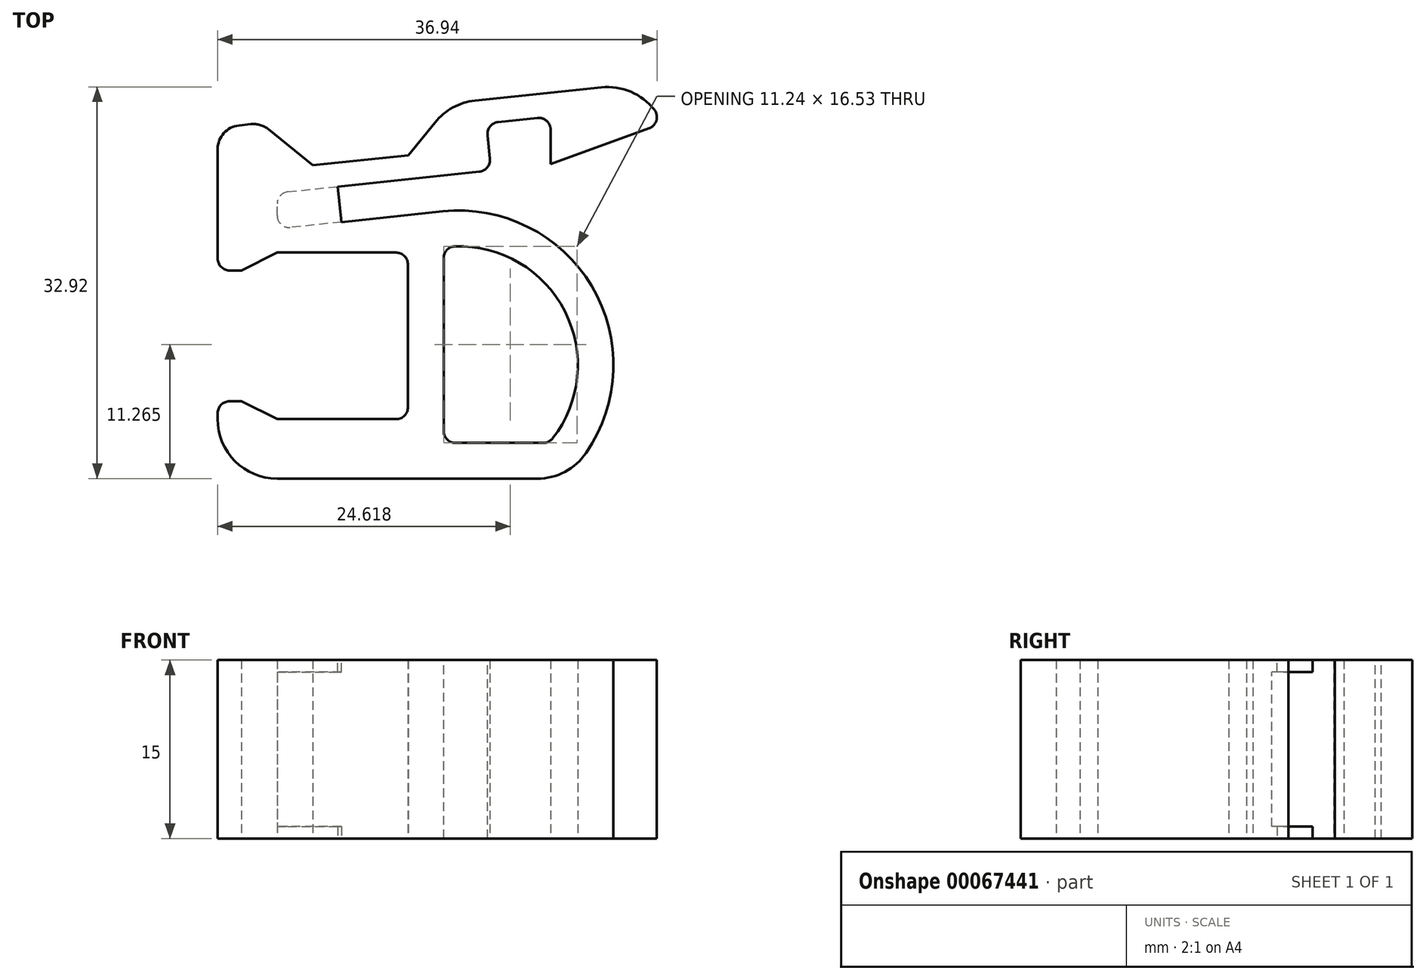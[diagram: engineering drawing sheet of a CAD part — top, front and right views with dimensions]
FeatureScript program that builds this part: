
annotation { "Feature Type Name" : "Feature", "Feature Type Description" : "" }
export const myFeature = defineFeature(function(context is Context, id is Id, definition is map)
    precondition{}
    {
        {
            var Q0;
            Q0=qCreatedBy(makeId("Top.planeOp"),FACE);
            var sketch = newSketch(context, id + "F0", { "sketchPlane" : qUnion([Q0])});
            skLineSegment(sketch, "E0", {"start": v(12, 7.43) * mm, "end": v(21.4, 10.85) * mm});
            skLineSegment(sketch, "E1", {"start": v(21.4, 10.85) * mm, "end": v(21.4, 14.43) * mm});
            skLineSegment(sketch, "E2", {"start": v(21.4, 14.43) * mm, "end": v(3.58, 12.56) * mm});
            skLineSegment(sketch, "E3", {"start": v(-16, 10.5) * mm, "end": v(-16, -1.5) * mm});
            skLineSegment(sketch, "E4", {"start": v(-16, -1.5) * mm, "end": v(-14, -1.5) * mm});
            skLineSegment(sketch, "E5", {"start": v(-14, -1.5) * mm, "end": v(-11, 0) * mm});
            skLineSegment(sketch, "E6", {"start": v(-11, 0) * mm, "end": v(0, 0) * mm});
            skLineSegment(sketch, "E7", {"start": v(0, 0) * mm, "end": v(0, -14) * mm});
            skLineSegment(sketch, "E8", {"start": v(0, -14) * mm, "end": v(-11, -14) * mm});
            skLineSegment(sketch, "E9", {"start": v(-11, -14) * mm, "end": v(-14, -12.5) * mm});
            skLineSegment(sketch, "E10", {"start": v(-14, -12.5) * mm, "end": v(-16, -12.5) * mm});
            skLineSegment(sketch, "E11", {"start": v(-16, -12.5) * mm, "end": v(-16, -19) * mm});
            skLineSegment(sketch, "E12", {"start": v(-16, -19) * mm, "end": v(13.12, -19) * mm});
            skLineSegment(sketch, "E13", {"start": v(2.92, 3.46) * mm, "end": v(-11, 2) * mm});
            skLineSegment(sketch, "E14", {"start": v(-11, 2) * mm, "end": v(-11, 5.02) * mm});
            skLineSegment(sketch, "E15", {"start": v(-11, 5.02) * mm, "end": v(7, 6.9) * mm});
            skLineSegment(sketch, "E16", {"start": v(7, 6.9) * mm, "end": v(6.58, 10.86) * mm});
            skLineSegment(sketch, "E17", {"start": v(6.58, 10.86) * mm, "end": v(12, 11.43) * mm});
            skLineSegment(sketch, "E18", {"start": v(12, 11.43) * mm, "end": v(12, 7.43) * mm});
            skArc(sketch, "E19", {"start": v(13.12, -19) * mm, "mid": v(16.12, -4.1) * mm, "end": v(2.92, 3.46) * mm});
            skArc(sketch, "E20.0", {"start": v(11.85, -16) * mm, "mid": v(13.09, -4.73) * mm, "end": v(3, 0.45) * mm});
            skLineSegment(sketch, "E21", {"start": v(3, 0.45) * mm, "end": v(3, -16) * mm});
            skLineSegment(sketch, "E22", {"start": v(3, -16) * mm, "end": v(11.85, -16) * mm});
            skLineSegment(sketch, "E23", {"start": v(-12.37, 10.88) * mm, "end": v(-8, 7.34) * mm});
            skLineSegment(sketch, "E24", {"start": v(-8, 7.34) * mm, "end": v(0.04, 8.19) * mm});
            skLineSegment(sketch, "E25", {"start": v(0.04, 8.19) * mm, "end": v(3.58, 12.56) * mm});
            skLineSegment(sketch, "E26.trimOffspring", {"start": v(-12.37, 10.88) * mm, "end": v(-16, 10.5) * mm});
            skSolve(sketch);
        }
        {
            var Q0;
            Q0=qSketchRegion(id+"F0",true);
            extrude(context, id + "F1", {"entities" : qUnion([Q0]), "endBound" : BoundingType.SYMMETRIC, "depth" : 15 * mm});
        }
        {
            var Q0;
            Q0=makeQuery(id+"F1.opExtrude","SWEPT_EDGE",EDGE,{"disambiguationData":[OSD([sQuery(id+"F0.wireOp",EDGE,"E1"),sQuery(id+"F0.wireOp",EDGE,"E2")])]});
            var Q1;
            Q1=makeQuery(id+"F1.opExtrude","SWEPT_EDGE",EDGE,{"disambiguationData":[OSD([sQuery(id+"F0.wireOp",EDGE,"E2"),sQuery(id+"F0.wireOp",EDGE,"E25")])]});
            var Q2;
            Q2=makeQuery(id+"F1.opExtrude","SWEPT_EDGE",EDGE,{"disambiguationData":[OSD([sQuery(id+"F0.wireOp",EDGE,"E1"),sQuery(id+"F0.wireOp",EDGE,"E2")])]});
            var Q3;
            Q3=makeQuery(id+"F1.opExtrude","SWEPT_EDGE",EDGE,{"disambiguationData":[OSD([sQuery(id+"F0.wireOp",EDGE,"E11"),sQuery(id+"F0.wireOp",EDGE,"E12")])]});
            var Q4;
            Q4=makeQuery(id+"F1.opExtrude","SWEPT_EDGE",EDGE,{"disambiguationData":[OSD([sQuery(id+"F0.wireOp",EDGE,"E12"),sQuery(id+"F0.wireOp",EDGE,"E19")])]});
            fillet(context, id + "F2", {"entities" : qUnion([Q0, Q1, Q2, Q3, Q4]), "radius" : 5 * mm, "tangentPropagation" : true, "allowEdgeOverflow" : false});
        }
        {
            var Q0;
            Q0=makeQuery(id+"F2.opFillet","BLEND_EDGE",EDGE,{"blendedFrom":[makeQuery(id+"F1.opExtrude","SWEPT_EDGE",EDGE,{"disambiguationData":[OSD([sQuery(id+"F0.wireOp",EDGE,"E1"),sQuery(id+"F0.wireOp",EDGE,"E2")])]}),makeQuery(id+"F1.opExtrude","SWEPT_FACE",FACE,{"disambiguationData":[OSD([sQuery(id+"F0.wireOp",EDGE,"E0")])]})],"blendedInto":[makeQuery(id+"F1.opExtrude","SWEPT_FACE",FACE,{"disambiguationData":[OSD([sQuery(id+"F0.wireOp",EDGE,"E0")])]})]});
            var Q1;
            Q1=makeQuery(id+"F1.opExtrude","SWEPT_EDGE",EDGE,{"disambiguationData":[OSD([sQuery(id+"F0.wireOp",EDGE,"E15"),sQuery(id+"F0.wireOp",EDGE,"E16")])]});
            var Q2;
            Q2=makeQuery(id+"F1.opExtrude","SWEPT_EDGE",EDGE,{"disambiguationData":[OSD([sQuery(id+"F0.wireOp",EDGE,"E14"),sQuery(id+"F0.wireOp",EDGE,"E15")])]});
            var Q3;
            Q3=makeQuery(id+"F1.opExtrude","SWEPT_EDGE",EDGE,{"disambiguationData":[OSD([sQuery(id+"F0.wireOp",EDGE,"E13"),sQuery(id+"F0.wireOp",EDGE,"E14")])]});
            var Q4;
            Q4=makeQuery(id+"F1.opExtrude","SWEPT_EDGE",EDGE,{"disambiguationData":[OSD([sQuery(id+"F0.wireOp",EDGE,"E17"),sQuery(id+"F0.wireOp",EDGE,"E18")])]});
            var Q5;
            Q5=makeQuery(id+"F1.opExtrude","SWEPT_EDGE",EDGE,{"disambiguationData":[OSD([sQuery(id+"F0.wireOp",EDGE,"E16"),sQuery(id+"F0.wireOp",EDGE,"E17")])]});
            var Q6;
            Q6=makeQuery(id+"F1.opExtrude","SWEPT_EDGE",EDGE,{"disambiguationData":[OSD([sQuery(id+"F0.wireOp",EDGE,"E6"),sQuery(id+"F0.wireOp",EDGE,"E7")])]});
            var Q7;
            Q7=makeQuery(id+"F1.opExtrude","SWEPT_EDGE",EDGE,{"disambiguationData":[OSD([sQuery(id+"F0.wireOp",EDGE,"E7"),sQuery(id+"F0.wireOp",EDGE,"E8")])]});
            var Q8;
            Q8=makeQuery(id+"F1.opExtrude","SWEPT_EDGE",EDGE,{"disambiguationData":[OSD([sQuery(id+"F0.wireOp",EDGE,"E20.0"),sQuery(id+"F0.wireOp",EDGE,"E22")])]});
            var Q9;
            Q9=makeQuery(id+"F1.opExtrude","SWEPT_EDGE",EDGE,{"disambiguationData":[OSD([sQuery(id+"F0.wireOp",EDGE,"E21"),sQuery(id+"F0.wireOp",EDGE,"E22")])]});
            var Q10;
            Q10=makeQuery(id+"F1.opExtrude","SWEPT_EDGE",EDGE,{"disambiguationData":[OSD([sQuery(id+"F0.wireOp",EDGE,"E20.0"),sQuery(id+"F0.wireOp",EDGE,"E21")])]});
            var Q11;
            Q11=makeQuery(id+"F1.opExtrude","SWEPT_EDGE",EDGE,{"disambiguationData":[OSD([sQuery(id+"F0.wireOp",EDGE,"E10"),sQuery(id+"F0.wireOp",EDGE,"E11")])]});
            var Q12;
            Q12=makeQuery(id+"F1.opExtrude","SWEPT_EDGE",EDGE,{"disambiguationData":[OSD([sQuery(id+"F0.wireOp",EDGE,"E3"),sQuery(id+"F0.wireOp",EDGE,"E4")])]});
            fillet(context, id + "F3", {"entities" : qUnion([Q0, Q1, Q2, Q3, Q4, Q5, Q6, Q7, Q8, Q9, Q10, Q11, Q12]), "radius" : 1 * mm, "tangentPropagation" : true, "allowEdgeOverflow" : false});
        }
        {
            var Q0;
            Q0=makeQuery(id+"F1.opExtrude","CAP_FACE",FACE,{"disambiguationData":[OSD([sQuery(id+"F0.wireOp",EDGE,"E0"),sQuery(id+"F0.wireOp",EDGE,"E1"),sQuery(id+"F0.wireOp",EDGE,"E2"),sQuery(id+"F0.wireOp",EDGE,"E3"),sQuery(id+"F0.wireOp",EDGE,"E4"),sQuery(id+"F0.wireOp",EDGE,"E5"),sQuery(id+"F0.wireOp",EDGE,"E6"),sQuery(id+"F0.wireOp",EDGE,"E7"),sQuery(id+"F0.wireOp",EDGE,"E8"),sQuery(id+"F0.wireOp",EDGE,"E9"),sQuery(id+"F0.wireOp",EDGE,"E10"),sQuery(id+"F0.wireOp",EDGE,"E11"),sQuery(id+"F0.wireOp",EDGE,"E12"),sQuery(id+"F0.wireOp",EDGE,"E13"),sQuery(id+"F0.wireOp",EDGE,"E14"),sQuery(id+"F0.wireOp",EDGE,"E15"),sQuery(id+"F0.wireOp",EDGE,"E16"),sQuery(id+"F0.wireOp",EDGE,"E17"),sQuery(id+"F0.wireOp",EDGE,"E18"),sQuery(id+"F0.wireOp",EDGE,"E19"),sQuery(id+"F0.wireOp",EDGE,"E20.0"),sQuery(id+"F0.wireOp",EDGE,"E21"),sQuery(id+"F0.wireOp",EDGE,"E22")])],"isStart":false});
            var sketch = newSketch(context, id + "F4", { "sketchPlane" : qUnion([Q0])});
            skLineSegment(sketch, "E27.0", {"start": v(-10.1, 5.11) * mm, "end": v(6, 6.8) * mm});
            skArc(sketch, "E28.0", {"start": v(-11, 4.12) * mm, "mid": v(-10.74, 4.79) * mm, "end": v(-10.1, 5.11) * mm});
            skLineSegment(sketch, "E29.0", {"start": v(-11, 3.11) * mm, "end": v(-11, 4.12) * mm});
            skArc(sketch, "E30.0", {"start": v(-9.9, 2.12) * mm, "mid": v(-10.67, 2.37) * mm, "end": v(-11, 3.11) * mm});
            skLineSegment(sketch, "E31.0", {"start": v(2.92, 3.46) * mm, "end": v(-9.9, 2.12) * mm});
            skLineSegment(sketch, "E32", {"start": v(-5.9, 5.55) * mm, "end": v(-5.59, 2.57) * mm});
            skSolve(sketch);
        }
        {
            var Q0;
            Q0=qSketchRegion(id+"F4",true);
            extrude(context, id + "F5", {"entities" : qUnion([Q0]), "oppositeDirection" : true, "depth" : 1 * mm});
        }
        {
            var Q0;
            Q0=makeQuery(id+"F5.opExtrude","SWEPT_BODY",BODY,{"disambiguationData":[OSD([sQuery(id+"F4.wireOp",EDGE,"E27.0"),sQuery(id+"F4.wireOp",EDGE,"E28.0"),sQuery(id+"F4.wireOp",EDGE,"E29.0"),sQuery(id+"F4.wireOp",EDGE,"E30.0"),sQuery(id+"F4.wireOp",EDGE,"E31.0"),sQuery(id+"F4.wireOp",EDGE,"E32")])]});
            var Q1;
            Q1=qCreatedBy(makeId("Top.planeOp"),FACE);
            mirror(context, id + "F6", {"operationType" : NewBodyOperationType.ADD, "entities" : qUnion([Q0]), "mirrorPlane" : qUnion([Q1])});
        }
        {
            var Q0;
            Q0=makeQuery(id+"F2.opFillet","BLEND_EDGE",EDGE,{"blendedFrom":[makeQuery(id+"F1.opExtrude","SWEPT_EDGE",EDGE,{"disambiguationData":[OSD([sQuery(id+"F0.wireOp",EDGE,"E3"),sQuery(id+"F0.wireOp",EDGE,"E26.trimOffspring")])]}),makeQuery(id+"F1.opExtrude","SWEPT_FACE",FACE,{"disambiguationData":[OSD([sQuery(id+"F0.wireOp",EDGE,"E23")])]})],"blendedInto":[makeQuery(id+"F1.opExtrude","SWEPT_FACE",FACE,{"disambiguationData":[OSD([sQuery(id+"F0.wireOp",EDGE,"E23")])]})]});
            var Q1;
            Q1=makeQuery(id+"F1.opExtrude","SWEPT_EDGE",EDGE,{"disambiguationData":[OSD([sQuery(id+"F0.wireOp",EDGE,"E23"),sQuery(id+"F0.wireOp",EDGE,"E26.trimOffspring")])]});
            var Q2;
            Q2=makeQuery(id+"F1.opExtrude","SWEPT_EDGE",EDGE,{"disambiguationData":[OSD([sQuery(id+"F0.wireOp",EDGE,"E3"),sQuery(id+"F0.wireOp",EDGE,"E26.trimOffspring")])]});
            fillet(context, id + "F7", {"entities" : qUnion([Q0, Q1, Q2]), "radius" : 2 * mm, "tangentPropagation" : true, "allowEdgeOverflow" : false});
        }
    });
